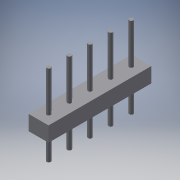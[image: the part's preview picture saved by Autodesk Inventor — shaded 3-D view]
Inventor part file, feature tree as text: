
AUTODESK INVENTOR PART (.ipt)
format: ipt  version: 2019.4 (Build 234330000, 330)  size: 117,760 bytes
history: native  units: mm
features: extrude x2, sketch x2, pattern_linear x1, projected_geometry x1
ambient origin geometry x8: Origin, YZ Plane, XZ Plane, XY Plane, X Axis, Y Axis, Z Axis, Center Point
bodies: Solid1 (feature_tree)
feature tree (6):
  extrude  "Extrusion1"  Depth=12.65mm
  extrude  "Extrusion2"  Depth=5.0mm
  pattern_linear  "Rectangular Pattern1"  Spacing1=5.0mm  [1 undecoded]
  sketch  "Sketch1"  dims[d0=2.45mm d1=12.65mm]
  sketch  "Sketch2"  dims[d2=1.84mm d3=0.0mm d4=0.5mm d5=5.0mm d6=5.0mm d7=0.0mm d8=0.0mm d9=50.0mm d11=2.54mm]
  projected_geometry  "Projected Loop1"
note: 1 required parameter value undecoded (feature->parameter linkage not recoverable at this tier; creation-order binding heuristic only, values carry confidence <= 0.55)
